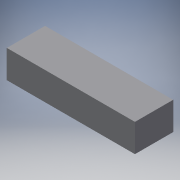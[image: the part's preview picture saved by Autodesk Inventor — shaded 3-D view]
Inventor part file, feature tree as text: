
AUTODESK INVENTOR PART (.ipt)
format: ipt  version: 2016 (Build 200138000, 138)  size: 92,160 bytes
history: native  units: mm
features: other x1, extrude x1, sketch x1
ambient origin geometry x8: Origin, YZ Plane, XZ Plane, XY Plane, X Axis, Y Axis, Z Axis, Center Point
bodies: Solid1 (feature_tree)
feature tree (3):
  parser-record x1  (decoder bookkeeping rows leaked as tree rows — omitted from the tree; the rows remain in map.json)
  extrude  "Extrusion1"  [1 undecoded]
  sketch  "Sketch1"  dims[d3=0.0mm]
note: 1 required parameter value undecoded (feature->parameter linkage not recoverable at this tier; creation-order binding heuristic only, values carry confidence <= 0.55)
note: 1 file-system path scrubbed to <path> (originals preserved in map.json)
